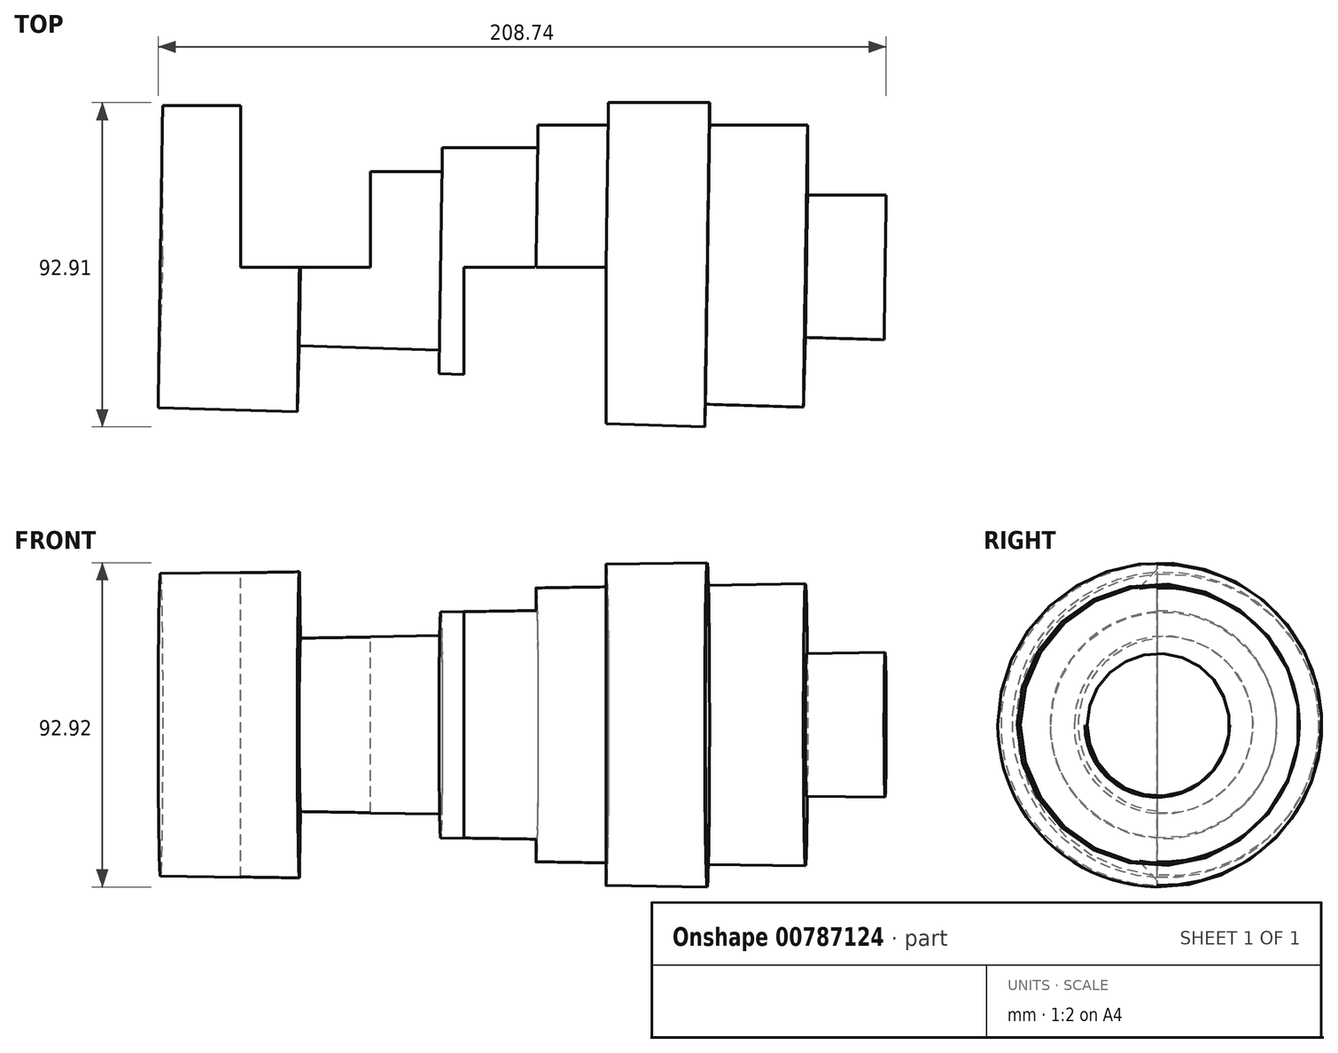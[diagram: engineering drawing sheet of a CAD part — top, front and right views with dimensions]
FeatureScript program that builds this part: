
annotation { "Feature Type Name" : "Feature", "Feature Type Description" : "" }
export const myFeature = defineFeature(function(context is Context, id is Id, definition is map)
    precondition{}
    {
        {
            var Q0;
            Q0=qCreatedBy(makeId("Top.planeOp"),FACE);
            var sketch = newSketch(context, id + "F0", { "sketchPlane" : qUnion([Q0])});
            skLineSegment(sketch, "E0", {"start": v(-59.53, 46.42) * mm, "end": v(-19.62, 46.42) * mm});
            skLineSegment(sketch, "E1", {"start": v(-19.62, 27.46) * mm, "end": v(20.68, 27.46) * mm});
            skLineSegment(sketch, "E2", {"start": v(20.68, 34.28) * mm, "end": v(48.12, 34.28) * mm});
            skLineSegment(sketch, "E3", {"start": v(48.12, 40.76) * mm, "end": v(68.31, 40.76) * mm});
            skLineSegment(sketch, "E4", {"start": v(68.31, 47.21) * mm, "end": v(97.28, 47.21) * mm});
            skLineSegment(sketch, "E5", {"start": v(97.28, 40.76) * mm, "end": v(125.38, 40.76) * mm});
            skLineSegment(sketch, "E6", {"start": v(125.38, 20.77) * mm, "end": v(147.92, 20.77) * mm});
            skLineSegment(sketch, "E7", {"start": v(-19.62, 46.42) * mm, "end": v(-19.62, 27.46) * mm});
            skLineSegment(sketch, "E8", {"start": v(20.68, 27.46) * mm, "end": v(20.68, 34.28) * mm});
            skLineSegment(sketch, "E9", {"start": v(48.12, 34.28) * mm, "end": v(48.12, 40.76) * mm});
            skLineSegment(sketch, "E10", {"start": v(68.31, 40.76) * mm, "end": v(68.31, 47.21) * mm});
            skLineSegment(sketch, "E11", {"start": v(97.28, 47.21) * mm, "end": v(97.28, 40.76) * mm});
            skLineSegment(sketch, "E12", {"start": v(125.38, 40.76) * mm, "end": v(125.38, 20.77) * mm});
            skLineSegment(sketch, "E13", {"start": v(-59.53, 46.42) * mm, "end": v(-59.53, 3.07) * mm});
            skLineSegment(sketch, "E14", {"start": v(-59.53, 3.07) * mm, "end": v(147.53, 0) * mm});
            skLineSegment(sketch, "E15", {"start": v(147.92, 20.77) * mm, "end": v(147.53, 0) * mm});
            skSolve(sketch);
        }
        {
            var Q0;
            Q0=makeQuery(id+"F0.imprint","IMPRINT",FACE,{"disambiguationData":[TD([[makeQuery(id+"F0.imprint","IMPRINT",EDGE,{"derivedFrom":sQuery(id+"F0.wireOp",EDGE,"E0")}),-1.0]])]});
            var Q1;
            Q1=sQuery(id+"F0.wireOp",EDGE,"E14");
            revolve(context, id + "F1", {"surfaceOperationType" : NewSurfaceOperationType.NEW, "entities" : qUnion([Q0]), "axis" : qUnion([Q1]), "revolveType" : RevolveType.FULL});
        }
        {
            var Q0;
            Q0=qCreatedBy(makeId("Front.planeOp"),FACE);
            var sketch = newSketch(context, id + "F2", { "sketchPlane" : qUnion([Q0])});
            skLineSegment(sketch, "E16.bottom", {"start": v(0, -78.1) * mm, "end": v(-37.17, -78.1) * mm});
            skLineSegment(sketch, "E16.top", {"start": v(0, 88.4) * mm, "end": v(-37.17, 88.4) * mm});
            skLineSegment(sketch, "E16.left", {"start": v(0, -78.1) * mm, "end": v(0, 88.4) * mm});
            skLineSegment(sketch, "E16.right", {"start": v(-37.17, -78.1) * mm, "end": v(-37.17, 88.4) * mm});
            skSolve(sketch);
        }
        {
            var Q0;
            Q0 = qSketchRegion(id + "F2", true);
            extrude(context, id + "F3", {"entities" : qUnion([Q0]), "operationType" : NewBodyOperationType.REMOVE, "oppositeDirection" : true, "depth" : 82.2 * mm, "offsetDistance" : 25 * mm});
        }
        {
            var Q0;
            Q0=qCreatedBy(makeId("Front.planeOp"),FACE);
            var sketch = newSketch(context, id + "F4", { "sketchPlane" : qUnion([Q0])});
            skLineSegment(sketch, "E17.bottom", {"start": v(67.63, 68.85) * mm, "end": v(26.85, 68.85) * mm});
            skLineSegment(sketch, "E17.top", {"start": v(67.63, -79.93) * mm, "end": v(26.85, -79.93) * mm});
            skLineSegment(sketch, "E17.left", {"start": v(67.63, 68.85) * mm, "end": v(67.63, -79.93) * mm});
            skLineSegment(sketch, "E17.right", {"start": v(26.85, 68.85) * mm, "end": v(26.85, -79.93) * mm});
            skSolve(sketch);
        }
        {
            var Q0;
            Q0 = qSketchRegion(id + "F4", true);
            extrude(context, id + "F5", {"entities" : qUnion([Q0]), "operationType" : NewBodyOperationType.REMOVE, "depth" : 98.6 * mm, "offsetDistance" : 25 * mm});
        }
    });
